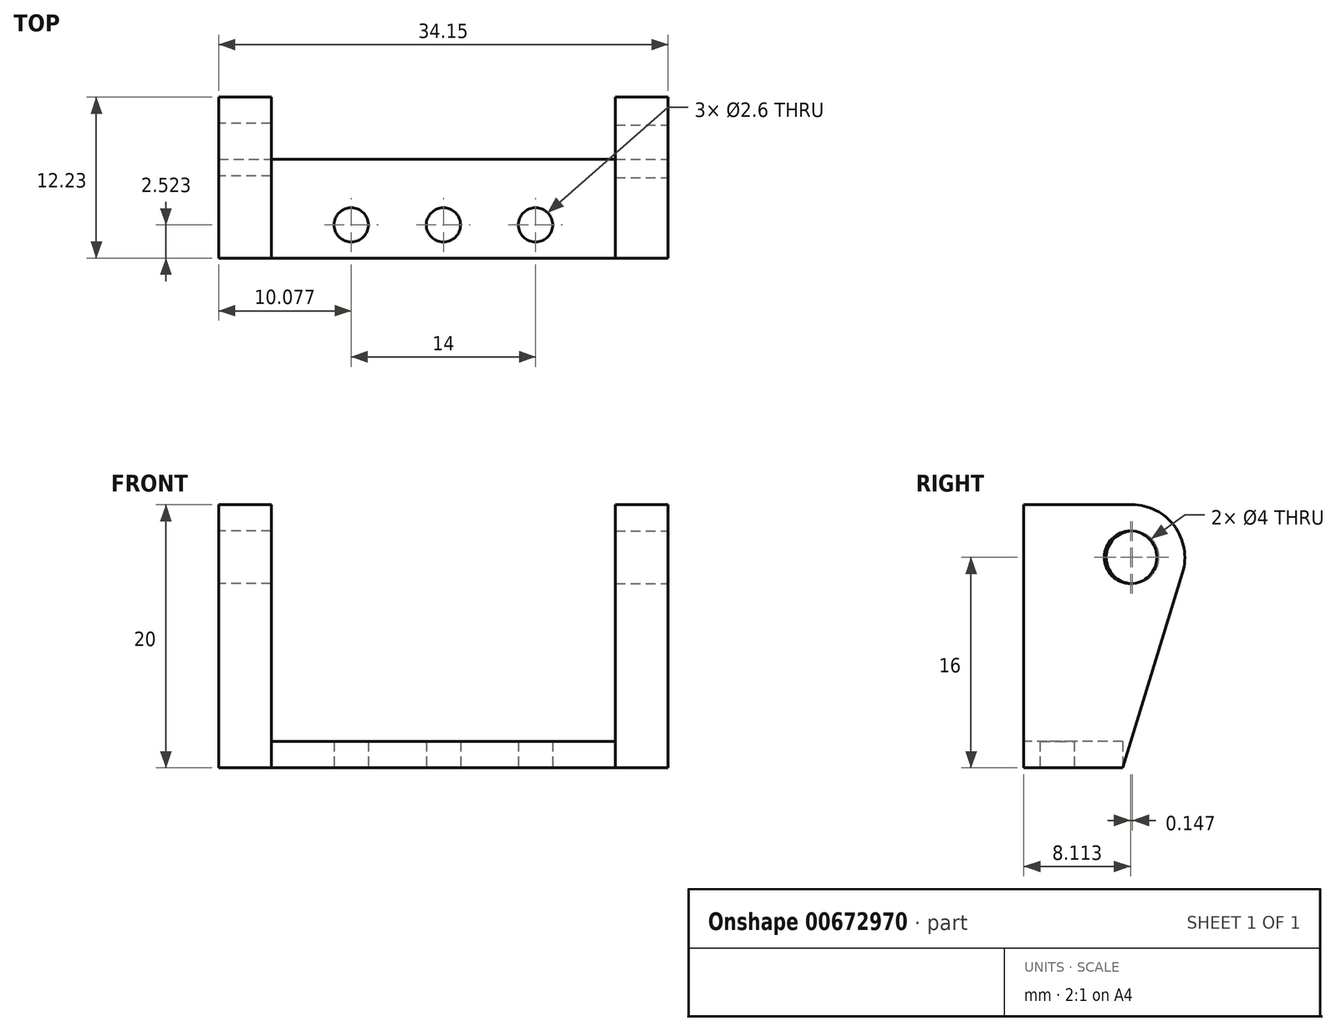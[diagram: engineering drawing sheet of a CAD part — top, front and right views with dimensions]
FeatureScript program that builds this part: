
annotation { "Feature Type Name" : "Feature", "Feature Type Description" : "" }
export const myFeature = defineFeature(function(context is Context, id is Id, definition is map)
    precondition{}
    {
        {
            var Q0;
            Q0=qCreatedBy(makeId("Top.planeOp"),FACE);
            var sketch = newSketch(context, id + "F0", { "sketchPlane" : qUnion([Q0])});
            skLineSegment(sketch, "E0.5", {"start": v(-2.39, -8.85) * mm, "end": v(-14.5, 0) * mm});
            skLineSegment(sketch, "E1", {"start": v(-16.55, 4.04) * mm, "end": v(-16.55, 11.56) * mm});
            skArc(sketch, "E2.filletArc", {"start": v(-16.55, 4.04) * mm, "mid": v(-16, 1.77) * mm, "end": v(-14.5, 0) * mm});
            skArc(sketch, "E3.filletArc", {"start": v(-2.39, -8.85) * mm, "mid": v(0.03, -9.79) * mm, "end": v(2.58, -9.39) * mm});
            skCircle(sketch, "E4", {"center": v(0.53, 6.56) * mm, "radius": 1.3 * mm});
            skLineSegment(sketch, "E5.MirrorCS", {"start": v(17.6, 4.04) * mm, "end": v(17.6, 11.56) * mm});
            skArc(sketch, "E6.MirrorCS", {"start": v(17.6, 4.04) * mm, "mid": v(17.54, 0.46) * mm, "end": v(15.11, -2.16) * mm});
            skLineSegment(sketch, "E7", {"start": v(2.58, -9.39) * mm, "end": v(15.11, -2.16) * mm});
            skCircle(sketch, "E8", {"center": v(-6.47, 6.56) * mm, "radius": 1.3 * mm});
            skCircle(sketch, "E9", {"center": v(7.53, 6.56) * mm, "radius": 1.3 * mm});
            skLineSegment(sketch, "E10", {"start": v(-16.55, 11.56) * mm, "end": v(17.6, 11.56) * mm});
            skLineSegment(sketch, "E11", {"start": v(17.6, 4.04) * mm, "end": v(-16.55, 4.04) * mm});
            skLineSegment(sketch, "E12", {"start": v(13.6, 11.56) * mm, "end": v(13.6, 4.04) * mm});
            skPoint(sketch, "E13.endSnap0", {"position": v(-16.55, 7.8) * mm});
            skLineSegment(sketch, "E14", {"start": v(13.6, 9.06) * mm, "end": v(17.6, 9.06) * mm, "construction": true});
            skLineSegment(sketch, "E15", {"start": v(-12.55, 11.56) * mm, "end": v(-12.55, 4.04) * mm});
            skLineSegment(sketch, "E16", {"start": v(-12.55, 8.8) * mm, "end": v(-16.55, 8.8) * mm, "construction": true});
            skLineSegment(sketch, "E17", {"start": v(-12.55, 9.1) * mm, "end": v(13.6, 9.06) * mm, "construction": true});
            skLineSegment(sketch, "E18", {"start": v(-16.55, 11.56) * mm, "end": v(-16.55, 16.56) * mm});
            skLineSegment(sketch, "E19", {"start": v(-16.55, 16.56) * mm, "end": v(-12.55, 16.56) * mm});
            skLineSegment(sketch, "E20", {"start": v(-12.55, 16.56) * mm, "end": v(-12.55, 11.56) * mm});
            skLineSegment(sketch, "E21", {"start": v(13.6, 11.56) * mm, "end": v(13.6, 16.56) * mm});
            skLineSegment(sketch, "E22", {"start": v(13.6, 16.56) * mm, "end": v(17.6, 16.56) * mm});
            skLineSegment(sketch, "E23", {"start": v(17.6, 16.56) * mm, "end": v(17.6, 11.56) * mm});
            skSolve(sketch);
        }
        {
            var Q0;
            {var subQ0=sQuery(id+"F0.wireOp",EDGE,"E1");Q0=makeQuery(id+"F0.imprint","IMPRINT",FACE,{"disambiguationData":[TD([[makeQuery(id+"F0.imprint","IMPRINT",EDGE,{"derivedFrom":subQ0}),-1.0]])]});}
            var Q1;
            {var subQ0=sQuery(id+"F0.wireOp",EDGE,"E5.MirrorCS");Q1=makeQuery(id+"F0.imprint","IMPRINT",FACE,{"disambiguationData":[TD([[makeQuery(id+"F0.imprint","IMPRINT",EDGE,{"derivedFrom":subQ0}),1.0]])]});}
            var Q2;
            {var subQ0=sQuery(id+"F0.wireOp",EDGE,"E18");Q2=makeQuery(id+"F0.imprint","IMPRINT",FACE,{"disambiguationData":[TD([[makeQuery(id+"F0.imprint","IMPRINT",EDGE,{"derivedFrom":subQ0}),-1.0]])]});}
            var Q3;
            {var subQ2=sQuery(id+"F0.wireOp",EDGE,"E21");Q3=makeQuery(id+"F0.imprint","IMPRINT",FACE,{"disambiguationData":[TD([[makeQuery(id+"F0.imprint","IMPRINT",EDGE,{"derivedFrom":subQ2}),-1.0]])]});}
            extrude(context, id + "F1", {"entities" : qUnion([Q0, Q1, Q2, Q3]), "depth" : 20 * mm, "offsetDistance" : 25 * mm});
        }
        {
            var Q0;
            Q0=makeQuery(id+"F0.imprint","IMPRINT",FACE,{"disambiguationData":[TD([[makeQuery(id+"F0.imprint","IMPRINT",EDGE,{"derivedFrom":sQuery(id+"F0.wireOp",EDGE,"E4")}),-1.0]])]});
            extrude(context, id + "F2", {"entities" : qUnion([Q0]), "depth" : 2 * mm, "offsetDistance" : 25 * mm});
        }
        {
            var Q0;
            Q0=makeQuery(id+"F1.opExtrude","CAP_EDGE",EDGE,{"disambiguationData":[OSD([sQuery(id+"F0.wireOp",EDGE,"E19")])],"isStart":true});
            chamfer(context, id + "F3", {"entities" : qUnion([Q0]), "chamferType" : ChamferType.OFFSET_ANGLE, "width" : 5 * mm, "oppositeDirection" : false, "angle" : 73 * degree, "tangentPropagation" : true});
        }
        {
            var Q0;
            Q0=makeQuery(id+"F1.opExtrude","CAP_EDGE",EDGE,{"disambiguationData":[OSD([sQuery(id+"F0.wireOp",EDGE,"E22")])],"isStart":true});
            chamfer(context, id + "F4", {"entities" : qUnion([Q0]), "chamferType" : ChamferType.OFFSET_ANGLE, "width" : 5 * mm, "oppositeDirection" : false, "angle" : 73 * degree, "tangentPropagation" : true});
        }
        {
            var Q0;
            Q0=makeQuery(id+"F1.opExtrude","SWEPT_FACE",FACE,{"disambiguationData":[OSD([sQuery(id+"F0.wireOp",EDGE,"E1"),sQuery(id+"F0.wireOp",EDGE,"E18")])]});
            var sketch = newSketch(context, id + "F5", { "sketchPlane" : qUnion([Q0])});
            skLineSegment(sketch, "E24", {"start": v(-7.8, 0) * mm, "end": v(-7.8, 2) * mm, "construction": true});
            skLineSegment(sketch, "E25", {"start": v(-7.8, 2) * mm, "end": v(-7.8, 16) * mm, "construction": true});
            skLineSegment(sketch, "E26", {"start": v(-7.8, 16) * mm, "end": v(-12.3, 16) * mm, "construction": true});
            skCircle(sketch, "E27", {"center": v(-12.3, 16) * mm, "radius": 2 * mm});
            skLineSegment(sketch, "E28", {"start": v(-7.8, 16) * mm, "end": v(-4.04, 16) * mm, "construction": true});
            skLineSegment(sketch, "E29", {"start": v(-12.3, 16) * mm, "end": v(-12.3, 20) * mm, "construction": true});
            skSolve(sketch);
        }
        {
            var Q0;
            Q0=makeQuery(id+"F5.imprint","IMPRINT",FACE,{"disambiguationData":[TD([[makeQuery(id+"F5.imprint","IMPRINT",EDGE,{"derivedFrom":sQuery(id+"F5.wireOp",EDGE,"E27")}),1.0]])]});
            extrude(context, id + "F6", {"entities" : qUnion([Q0]), "operationType" : NewBodyOperationType.REMOVE, "oppositeDirection" : true, "depth" : 5.8 * mm, "offsetDistance" : 25 * mm});
        }
        {
            var Q0;
            Q0=makeQuery(id+"F1.opExtrude","SWEPT_FACE",FACE,{"disambiguationData":[OSD([sQuery(id+"F0.wireOp",EDGE,"E5.MirrorCS"),sQuery(id+"F0.wireOp",EDGE,"E23")])]});
            var sketch = newSketch(context, id + "F7", { "sketchPlane" : qUnion([Q0])});
            skLineSegment(sketch, "E30", {"start": v(4.04, 16) * mm, "end": v(12.15, 16) * mm, "construction": true});
            skLineSegment(sketch, "E31", {"start": v(12.15, 16) * mm, "end": v(12.15, 20) * mm, "construction": true});
            skCircle(sketch, "E32", {"center": v(12.15, 16) * mm, "radius": 2 * mm});
            skSolve(sketch);
        }
        {
            var Q0;
            Q0=makeQuery(id+"F7.imprint","IMPRINT",FACE,{"disambiguationData":[TD([[makeQuery(id+"F7.imprint","IMPRINT",EDGE,{"derivedFrom":sQuery(id+"F7.wireOp",EDGE,"E32")}),1.0]])]});
            extrude(context, id + "F8", {"entities" : qUnion([Q0]), "operationType" : NewBodyOperationType.REMOVE, "oppositeDirection" : true, "depth" : 7.32 * mm, "offsetDistance" : 25 * mm});
        }
        {
            var Q0;
            Q0=makeQuery(id+"F1.opExtrude","CAP_EDGE",EDGE,{"disambiguationData":[OSD([sQuery(id+"F0.wireOp",EDGE,"E22")])],"isStart":false});
            var Q1;
            Q1=makeQuery(id+"F1.opExtrude","CAP_EDGE",EDGE,{"disambiguationData":[OSD([sQuery(id+"F0.wireOp",EDGE,"E19")])],"isStart":false});
            fillet(context, id + "F9", {"entities" : qUnion([Q0, Q1]), "radius" : 4 * mm, "tangentPropagation" : true, "allowEdgeOverflow" : false});
        }
        {
            var Q0;
            {var subQ0=sQuery(id+"F0.wireOp",EDGE,"E22");Q0=makeQuery(id+"F9.opFillet","BLEND_EDGE",EDGE,{"blendedFrom":[makeQuery(id+"F1.opExtrude","CAP_EDGE",EDGE,{"disambiguationData":[OSD([subQ0])],"isStart":false}),makeQuery(id+"F4.opChamfer","BLEND_FACE",FACE,{"disambiguationData":[OSD([subQ0])]})],"blendedInto":[makeQuery(id+"F4.opChamfer","BLEND_FACE",FACE,{"disambiguationData":[OSD([subQ0])]})]});}
            var Q1;
            {var subQ0=sQuery(id+"F0.wireOp",EDGE,"E19");Q1=makeQuery(id+"F9.opFillet","BLEND_EDGE",EDGE,{"blendedFrom":[makeQuery(id+"F1.opExtrude","CAP_EDGE",EDGE,{"disambiguationData":[OSD([subQ0])],"isStart":false}),makeQuery(id+"F3.opChamfer","BLEND_FACE",FACE,{"disambiguationData":[OSD([subQ0])]})],"blendedInto":[makeQuery(id+"F3.opChamfer","BLEND_FACE",FACE,{"disambiguationData":[OSD([subQ0])]})]});}
            fillet(context, id + "F10", {"entities" : qUnion([Q0, Q1]), "radius" : 4 * mm, "tangentPropagation" : true, "allowEdgeOverflow" : false});
        }
    });
